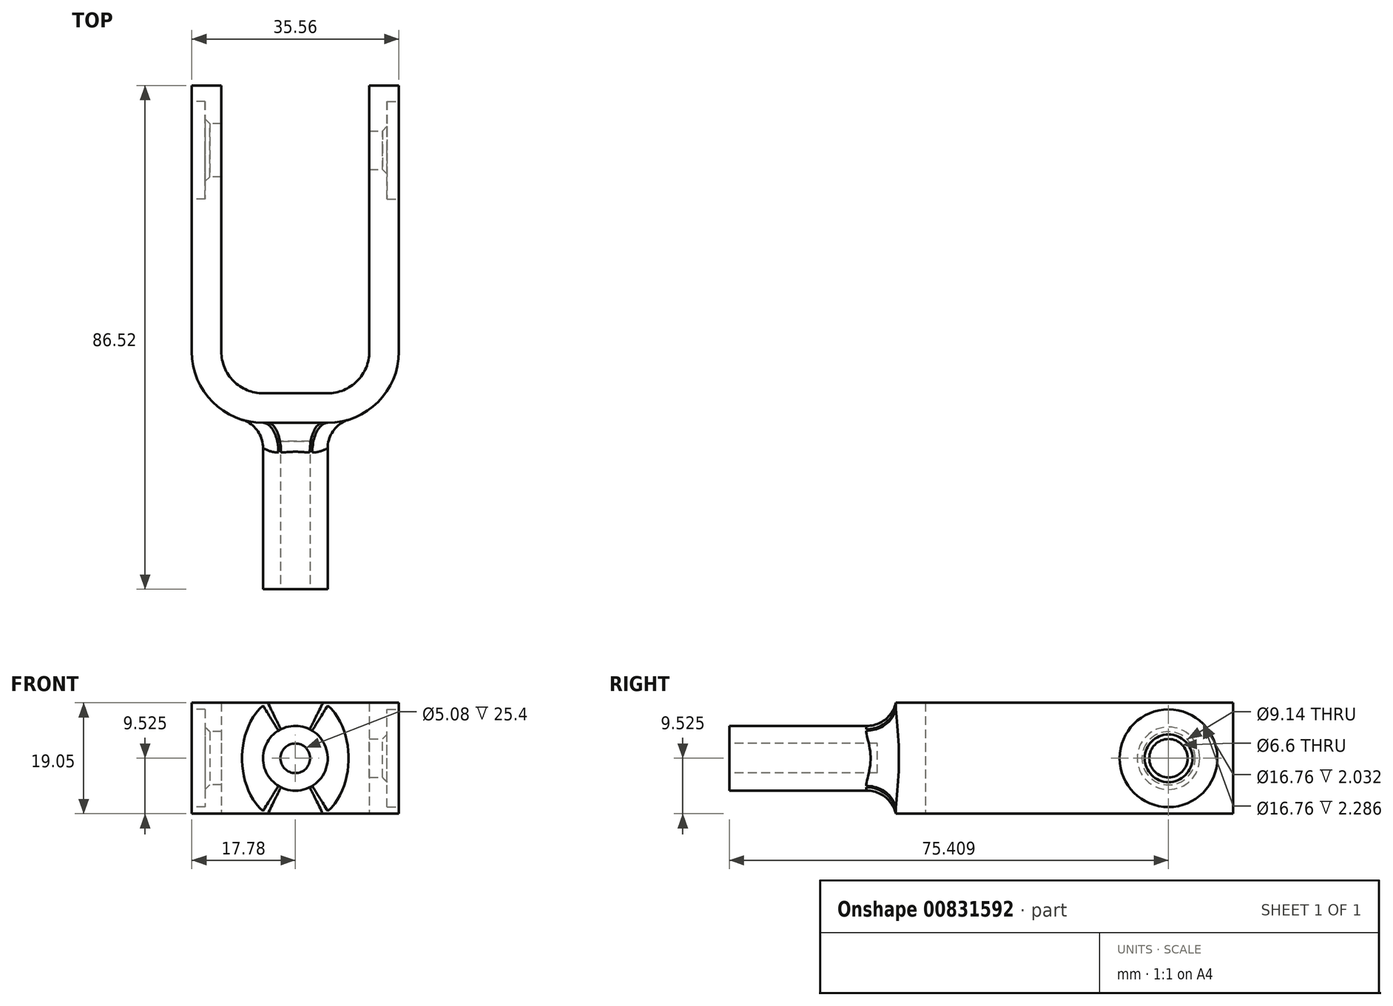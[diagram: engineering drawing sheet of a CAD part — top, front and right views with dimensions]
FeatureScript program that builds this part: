
annotation { "Feature Type Name" : "Feature", "Feature Type Description" : "" }
export const myFeature = defineFeature(function(context is Context, id is Id, definition is map)
    precondition{}
    {
        {
            var Q0;
            Q0=qCreatedBy(makeId("Top.planeOp"),FACE);
            var sketch = newSketch(context, id + "F0", { "sketchPlane" : qUnion([Q0])});
            skLineSegment(sketch, "E0.bottom", {"start": v(5.56, -26.43) * mm, "end": v(-5.56, -26.43) * mm});
            skLineSegment(sketch, "E0.left", {"start": v(12.7, -19.29) * mm, "end": v(12.7, 26.43) * mm});
            skLineSegment(sketch, "E0.right", {"start": v(-12.7, -19.29) * mm, "end": v(-12.7, 26.43) * mm});
            skPoint(sketch, "E0.middle", {"position": v(0, 0) * mm});
            skPoint(sketch, "E1.visualSharp", {"position": v(-12.7, -26.43) * mm});
            skArc(sketch, "E1.filletArc", {"start": v(-12.7, -19.29) * mm, "mid": v(-10.6, -24.34) * mm, "end": v(-5.56, -26.43) * mm});
            skPoint(sketch, "E2.visualSharp", {"position": v(12.7, -26.43) * mm});
            skArc(sketch, "E2.filletArc", {"start": v(5.56, -26.43) * mm, "mid": v(10.6, -24.34) * mm, "end": v(12.7, -19.29) * mm});
            skLineSegment(sketch, "E3.0", {"start": v(17.78, -19.29) * mm, "end": v(17.78, 26.43) * mm});
            skLineSegment(sketch, "E3.1", {"start": v(-17.78, -19.29) * mm, "end": v(-17.78, 26.43) * mm});
            skArc(sketch, "E3.2", {"start": v(-17.78, -19.29) * mm, "mid": v(-14.2, -27.93) * mm, "end": v(-5.56, -31.51) * mm});
            skLineSegment(sketch, "E3.3", {"start": v(5.56, -31.51) * mm, "end": v(-5.56, -31.51) * mm});
            skArc(sketch, "E3.4", {"start": v(5.56, -31.51) * mm, "mid": v(14.2, -27.93) * mm, "end": v(17.78, -19.29) * mm});
            skLineSegment(sketch, "E4", {"start": v(12.7, 26.43) * mm, "end": v(17.78, 26.43) * mm});
            skLineSegment(sketch, "E5", {"start": v(-12.7, 26.43) * mm, "end": v(-17.78, 26.43) * mm});
            skSolve(sketch);
        }
        {
            var Q0;
            Q0 = qSketchRegion(id + "F0", true);
            extrude(context, id + "F1", {"entities" : qUnion([Q0]), "depth" : 19.05 * mm, "offsetDistance" : 25.4 * mm});
        }
        {
            var Q0;
            Q0=makeQuery(id+"F1.opExtrude","SWEPT_FACE",FACE,{"disambiguationData":[OSD([sQuery(id+"F0.wireOp",EDGE,"E3.3")])]});
            var sketch = newSketch(context, id + "F2", { "sketchPlane" : qUnion([Q0])});
            skCircle(sketch, "E6", {"center": v(0, 9.53) * mm, "radius": 5.56 * mm});
            skSolve(sketch);
        }
        {
            var Q0;
            Q0 = qSketchRegion(id + "F2", true);
            extrude(context, id + "F3", {"entities" : qUnion([Q0]), "operationType" : NewBodyOperationType.ADD, "depth" : 28.57 * mm, "offsetDistance" : 25.4 * mm});
        }
        {
            var Q0;
            Q0=makeQuery(id+"F3.boolean.opBoolean","SPLIT",EDGE,{"disambiguationData":[OD(1.0)],"derivedFrom":makeQuery(id+"F3.opExtrude","CAP_EDGE",EDGE,{"disambiguationData":[OSD([sQuery(id+"F2.wireOp",EDGE,"E6")])],"isStart":true})});
            fillet(context, id + "F4", {"entities" : qUnion([Q0]), "radius" : 5.08 * mm, "tangentPropagation" : true, "allowEdgeOverflow" : false});
        }
        {
            var Q0;
            Q0=makeQuery(id+"F3.opExtrude","CAP_FACE",FACE,{"disambiguationData":[OSD([sQuery(id+"F2.wireOp",EDGE,"E6")])],"isStart":false});
            var sketch = newSketch(context, id + "F5", { "sketchPlane" : qUnion([Q0])});
            skCircle(sketch, "E7", {"center": v(0, 9.53) * mm, "radius": 2.54 * mm});
            skSolve(sketch);
        }
        {
            var Q0;
            Q0 = qSketchRegion(id + "F5", true);
            extrude(context, id + "F6", {"entities" : qUnion([Q0]), "operationType" : NewBodyOperationType.REMOVE, "oppositeDirection" : true, "depth" : 25.4 * mm, "offsetDistance" : 25.4 * mm});
        }
        {
            var Q0;
            Q0=makeQuery(id+"F1.opExtrude","SWEPT_FACE",FACE,{"disambiguationData":[OSD([sQuery(id+"F0.wireOp",EDGE,"E3.0")])]});
            var sketch = newSketch(context, id + "F7", { "sketchPlane" : qUnion([Q0])});
            skCircle(sketch, "E8", {"center": v(15.32, 9.53) * mm, "radius": 3.3 * mm});
            skSolve(sketch);
        }
        {
            var Q0;
            Q0 = qSketchRegion(id + "F7", true);
            extrude(context, id + "F8", {"entities" : qUnion([Q0]), "operationType" : NewBodyOperationType.REMOVE, "oppositeDirection" : true, "depth" : 5.08 * mm, "offsetDistance" : 25.4 * mm});
        }
        {
            var Q0;
            Q0=makeQuery(id+"F1.opExtrude","SWEPT_FACE",FACE,{"disambiguationData":[OSD([sQuery(id+"F0.wireOp",EDGE,"E3.0")])]});
            var sketch = newSketch(context, id + "F9", { "sketchPlane" : qUnion([Q0])});
            skCircle(sketch, "E9", {"center": v(15.32, 9.53) * mm, "radius": 8.38 * mm});
            skSolve(sketch);
        }
        {
            var Q0;
            Q0 = qSketchRegion(id + "F9", true);
            extrude(context, id + "F10", {"entities" : qUnion([Q0]), "operationType" : NewBodyOperationType.REMOVE, "oppositeDirection" : true, "depth" : 2.03 * mm, "offsetDistance" : 25.4 * mm});
        }
        {
            var Q0;
            Q0=makeQuery(id+"F1.opExtrude","SWEPT_FACE",FACE,{"disambiguationData":[OSD([sQuery(id+"F0.wireOp",EDGE,"E3.1")])]});
            var sketch = newSketch(context, id + "F11", { "sketchPlane" : qUnion([Q0])});
            skCircle(sketch, "E10", {"center": v(-15.32, 9.53) * mm, "radius": 4.57 * mm});
            skSolve(sketch);
        }
        {
            var Q0;
            Q0 = qSketchRegion(id + "F11", true);
            extrude(context, id + "F12", {"entities" : qUnion([Q0]), "operationType" : NewBodyOperationType.REMOVE, "oppositeDirection" : true, "depth" : 5.08 * mm, "offsetDistance" : 25.4 * mm});
        }
        {
            var Q0;
            Q0=makeQuery(id+"F1.opExtrude","SWEPT_FACE",FACE,{"disambiguationData":[OSD([sQuery(id+"F0.wireOp",EDGE,"E3.1")])]});
            var sketch = newSketch(context, id + "F13", { "sketchPlane" : qUnion([Q0])});
            skCircle(sketch, "E11", {"center": v(-15.32, 9.53) * mm, "radius": 8.38 * mm});
            skSolve(sketch);
        }
        {
            var Q0;
            Q0 = qSketchRegion(id + "F13", true);
            extrude(context, id + "F14", {"entities" : qUnion([Q0]), "operationType" : NewBodyOperationType.REMOVE, "oppositeDirection" : true, "depth" : 2.3 * mm, "offsetDistance" : 25.4 * mm});
        }
        {
            var Q0;
            Q0=makeQuery(id+"F10.boolean.opBoolean","INTERSECT",EDGE,{"derivedFrom":[makeQuery(id+"F8.boolean.opBoolean","COPY",FACE,{"derivedFrom":makeQuery(id+"F8.opExtrude","SWEPT_FACE",FACE,{"disambiguationData":[OSD([sQuery(id+"F7.wireOp",EDGE,"E8")])]})}),makeQuery(id+"F10.opExtrude","CAP_FACE",FACE,{"disambiguationData":[OSD([sQuery(id+"F9.wireOp",EDGE,"E9")])],"isStart":false})]});
            chamfer(context, id + "F15", {"entities" : qUnion([Q0]), "width" : 0.8 * mm, "tangentPropagation" : true});
        }
        {
            var Q0;
            Q0=makeQuery(id+"F14.boolean.opBoolean","INTERSECT",EDGE,{"derivedFrom":[makeQuery(id+"F12.boolean.opBoolean","COPY",FACE,{"derivedFrom":makeQuery(id+"F12.opExtrude","SWEPT_FACE",FACE,{"disambiguationData":[OSD([sQuery(id+"F11.wireOp",EDGE,"E10")])]})}),makeQuery(id+"F14.opExtrude","CAP_FACE",FACE,{"disambiguationData":[OSD([sQuery(id+"F13.wireOp",EDGE,"E11")])],"isStart":false})]});
            chamfer(context, id + "F16", {"entities" : qUnion([Q0]), "width" : 0.8 * mm, "tangentPropagation" : true});
        }
    });
